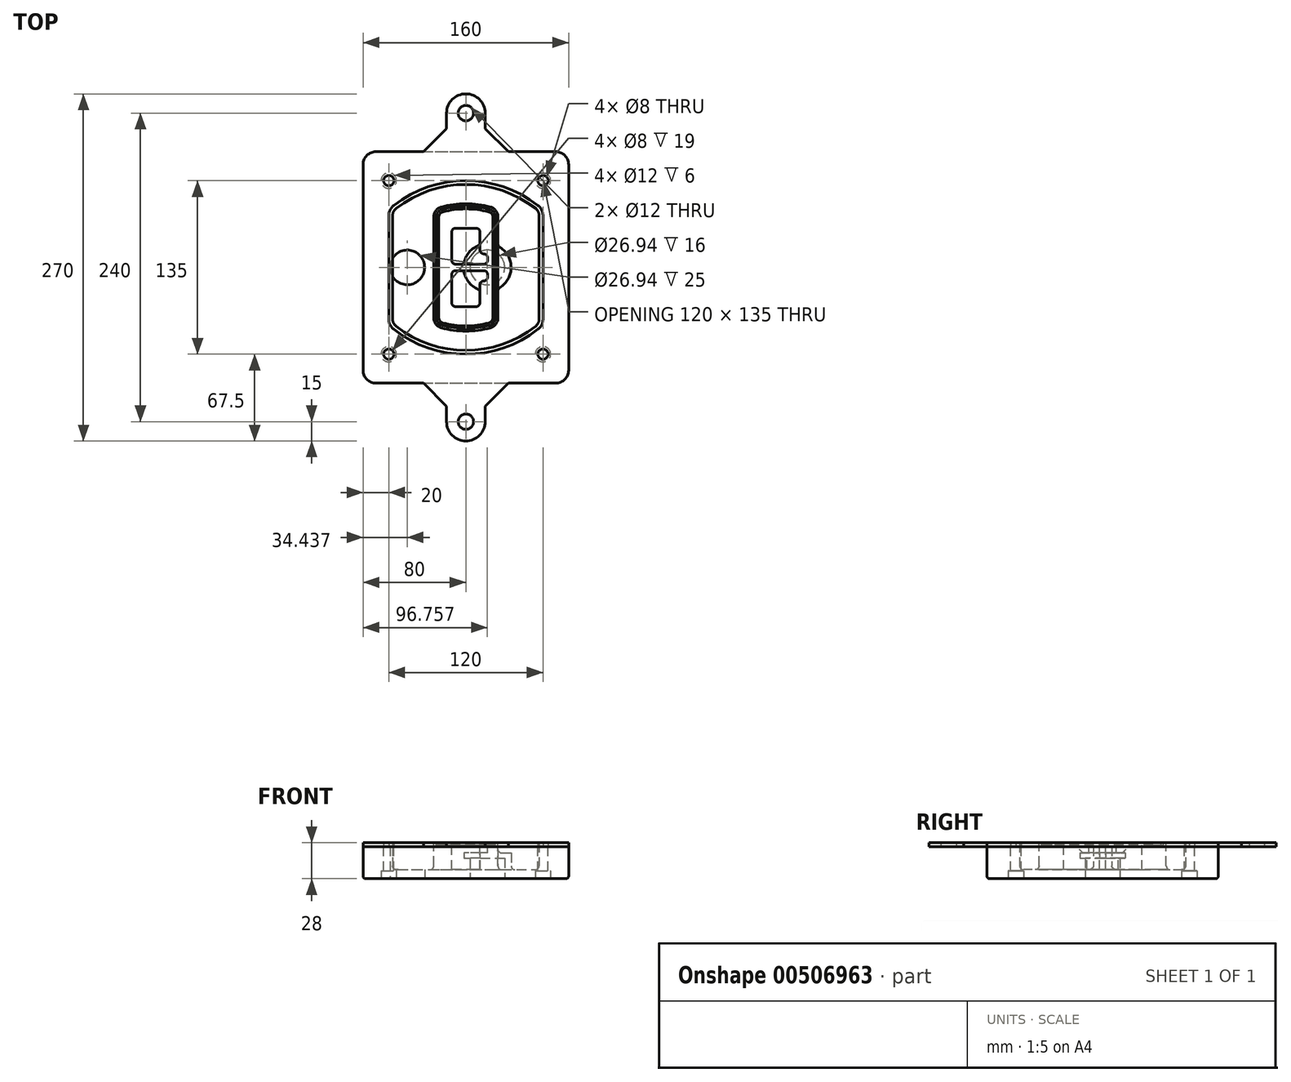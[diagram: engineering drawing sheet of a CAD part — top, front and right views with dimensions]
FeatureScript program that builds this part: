
annotation { "Feature Type Name" : "Feature", "Feature Type Description" : "" }
export const myFeature = defineFeature(function(context is Context, id is Id, definition is map)
    precondition{}
    {
        {
            var Q0;
            Q0=qCreatedBy(makeId("Top.planeOp"),FACE);
            var sketch = newSketch(context, id + "F0", { "sketchPlane" : qUnion([Q0])});
            skPoint(sketch, "E0.rect.middle", {"position": v(0, 0) * mm});
            skLineSegment(sketch, "E1.bottom", {"start": v(-70, -90) * mm, "end": v(70, -90) * mm});
            skLineSegment(sketch, "E1.top", {"start": v(-70, 90) * mm, "end": v(70, 90) * mm});
            skLineSegment(sketch, "E1.left", {"start": v(-80, -80) * mm, "end": v(-80, 80) * mm});
            skLineSegment(sketch, "E1.right", {"start": v(80, -80) * mm, "end": v(80, 80) * mm});
            skLineSegment(sketch, "E2", {"start": v(-80, 90) * mm, "end": v(80, -90) * mm, "construction": true});
            skLineSegment(sketch, "E3", {"start": v(80, 90) * mm, "end": v(-80, -90) * mm, "construction": true});
            skCircle(sketch, "E4", {"center": v(-60, 67.5) * mm, "radius": 4 * mm});
            skCircle(sketch, "E5", {"center": v(60, 67.5) * mm, "radius": 4 * mm});
            skCircle(sketch, "E6", {"center": v(60, -67.5) * mm, "radius": 4 * mm});
            skCircle(sketch, "E7", {"center": v(-60, -67.5) * mm, "radius": 4 * mm});
            skLineSegment(sketch, "E8", {"start": v(-60, 67.5) * mm, "end": v(60, 67.5) * mm, "construction": true});
            skLineSegment(sketch, "E9", {"start": v(60, 67.5) * mm, "end": v(60, -67.5) * mm, "construction": true});
            skLineSegment(sketch, "E10", {"start": v(60, -67.5) * mm, "end": v(-60, -67.5) * mm, "construction": true});
            skLineSegment(sketch, "E11", {"start": v(-60, -67.5) * mm, "end": v(-60, 67.5) * mm, "construction": true});
            skLineSegment(sketch, "E12", {"start": v(-60, 40.3) * mm, "end": v(-60, -40.3) * mm});
            skLineSegment(sketch, "E13", {"start": v(60, 40.3) * mm, "end": v(60, -40.3) * mm});
            skArc(sketch, "E14", {"start": v(56.15, 48.18) * mm, "mid": v(0, 67.5) * mm, "end": v(-56.15, 48.18) * mm});
            skArc(sketch, "E15", {"start": v(-56.15, -48.18) * mm, "mid": v(0, -67.5) * mm, "end": v(56.15, -48.18) * mm});
            skLineSegment(sketch, "E16", {"start": v(-60, 0) * mm, "end": v(60, 0) * mm, "construction": true});
            skPoint(sketch, "E17.visualSharp", {"position": v(-60, -45) * mm});
            skArc(sketch, "E17.filletArc", {"start": v(-60, -40.3) * mm, "mid": v(-58.99, -44.68) * mm, "end": v(-56.15, -48.18) * mm});
            skPoint(sketch, "E18.visualSharp", {"position": v(-60, 45) * mm});
            skArc(sketch, "E18.filletArc", {"start": v(-56.15, 48.18) * mm, "mid": v(-58.99, 44.68) * mm, "end": v(-60, 40.3) * mm});
            skPoint(sketch, "E19.visualSharp", {"position": v(60, 45) * mm});
            skArc(sketch, "E19.filletArc", {"start": v(60, 40.3) * mm, "mid": v(58.99, 44.68) * mm, "end": v(56.15, 48.18) * mm});
            skPoint(sketch, "E20.visualSharp", {"position": v(60, -45) * mm});
            skArc(sketch, "E20.filletArc", {"start": v(56.15, -48.18) * mm, "mid": v(58.99, -44.68) * mm, "end": v(60, -40.3) * mm});
            skPoint(sketch, "E21.visualSharp", {"position": v(-80, 90) * mm});
            skArc(sketch, "E21.filletArc", {"start": v(-70, 90) * mm, "mid": v(-77.07, 87.07) * mm, "end": v(-80, 80) * mm});
            skPoint(sketch, "E22.visualSharp", {"position": v(80, 90) * mm});
            skArc(sketch, "E22.filletArc", {"start": v(80, 80) * mm, "mid": v(77.07, 87.07) * mm, "end": v(70, 90) * mm});
            skPoint(sketch, "E23.visualSharp", {"position": v(80, -90) * mm});
            skArc(sketch, "E23.filletArc", {"start": v(70, -90) * mm, "mid": v(77.07, -87.07) * mm, "end": v(80, -80) * mm});
            skPoint(sketch, "E24.visualSharp", {"position": v(-80, -90) * mm});
            skArc(sketch, "E24.filletArc", {"start": v(-80, -80) * mm, "mid": v(-77.07, -87.07) * mm, "end": v(-70, -90) * mm});
            skArc(sketch, "E25.0", {"start": v(57, 40.3) * mm, "mid": v(56.3, 43.36) * mm, "end": v(54.3, 45.81) * mm});
            skLineSegment(sketch, "E25.1", {"start": v(57, 40.3) * mm, "end": v(57, -40.3) * mm});
            skArc(sketch, "E25.2", {"start": v(54.3, -45.81) * mm, "mid": v(56.3, -43.36) * mm, "end": v(57, -40.3) * mm});
            skArc(sketch, "E25.3", {"start": v(-54.3, -45.81) * mm, "mid": v(0, -64.5) * mm, "end": v(54.3, -45.81) * mm});
            skArc(sketch, "E25.4", {"start": v(-57, -40.3) * mm, "mid": v(-56.3, -43.36) * mm, "end": v(-54.3, -45.81) * mm});
            skArc(sketch, "E25.5", {"start": v(54.3, 45.81) * mm, "mid": v(0, 64.5) * mm, "end": v(-54.3, 45.81) * mm});
            skLineSegment(sketch, "E25.6", {"start": v(-57, 40.3) * mm, "end": v(-57, -40.3) * mm});
            skArc(sketch, "E25.7", {"start": v(-54.3, 45.81) * mm, "mid": v(-56.3, 43.36) * mm, "end": v(-57, 40.3) * mm});
            skArc(sketch, "E26.0", {"start": v(-58.62, 51.33) * mm, "mid": v(-62.58, 46.43) * mm, "end": v(-64, 40.3) * mm});
            skArc(sketch, "E26.1", {"start": v(58.62, 51.33) * mm, "mid": v(0, 71.5) * mm, "end": v(-58.62, 51.33) * mm});
            skArc(sketch, "E26.2", {"start": v(64, 40.3) * mm, "mid": v(62.58, 46.43) * mm, "end": v(58.62, 51.33) * mm});
            skLineSegment(sketch, "E26.3", {"start": v(64, 40.3) * mm, "end": v(64, -40.3) * mm});
            skArc(sketch, "E26.4", {"start": v(58.62, -51.33) * mm, "mid": v(62.58, -46.43) * mm, "end": v(64, -40.3) * mm});
            skLineSegment(sketch, "E26.5", {"start": v(-64, 40.3) * mm, "end": v(-64, -40.3) * mm});
            skArc(sketch, "E26.6", {"start": v(-58.62, -51.33) * mm, "mid": v(0, -71.5) * mm, "end": v(58.62, -51.33) * mm});
            skArc(sketch, "E26.7", {"start": v(-64, -40.3) * mm, "mid": v(-62.58, -46.43) * mm, "end": v(-58.62, -51.33) * mm});
            skSolve(sketch);
        }
        {
            var Q0;
            Q0=makeQuery(id+"F0.imprint","IMPRINT",FACE,{"disambiguationData":[TD([[makeQuery(id+"F0.imprint","IMPRINT",EDGE,{"derivedFrom":sQuery(id+"F0.wireOp",EDGE,"E1.bottom")}),1.0]])]});
            var Q1;
            Q1=makeQuery(id+"F0.imprint","IMPRINT",FACE,{"disambiguationData":[TD([[makeQuery(id+"F0.imprint","IMPRINT",EDGE,{"derivedFrom":sQuery(id+"F0.wireOp",EDGE,"E12")}),1.0]])]});
            var Q2;
            Q2=makeQuery(id+"F0.imprint","IMPRINT",FACE,{"disambiguationData":[TD([[makeQuery(id+"F0.imprint","IMPRINT",EDGE,{"derivedFrom":sQuery(id+"F0.wireOp",EDGE,"E25.0")}),1.0]])]});
            var Q3;
            Q3=makeQuery(id+"F0.imprint","IMPRINT",FACE,{"disambiguationData":[TD([[makeQuery(id+"F0.imprint","IMPRINT",EDGE,{"derivedFrom":sQuery(id+"F0.wireOp",EDGE,"E12")}),-1.0]])]});
            extrude(context, id + "F1", {"entities" : qUnion([Q0, Q1, Q2, Q3]), "oppositeDirection" : true, "depth" : 25 * mm});
        }
        {
            var Q0;
            Q0=makeQuery(id+"F0.imprint","IMPRINT",FACE,{"disambiguationData":[TD([[makeQuery(id+"F0.imprint","IMPRINT",EDGE,{"derivedFrom":sQuery(id+"F0.wireOp",EDGE,"E12")}),1.0]])]});
            extrude(context, id + "F2", {"entities" : qUnion([Q0]), "operationType" : NewBodyOperationType.ADD, "depth" : 3 * mm});
        }
        {
            var Q0;
            Q0=makeQuery(id+"F0.imprint","IMPRINT",FACE,{"disambiguationData":[TD([[makeQuery(id+"F0.imprint","IMPRINT",EDGE,{"derivedFrom":sQuery(id+"F0.wireOp",EDGE,"E25.0")}),1.0]])]});
            extrude(context, id + "F3", {"entities" : qUnion([Q0]), "operationType" : NewBodyOperationType.REMOVE, "oppositeDirection" : true, "depth" : 18 * mm});
        }
        {
            var Q0;
            Q0=makeQuery(id+"F2.opExtrude","CAP_FACE",FACE,{"disambiguationData":[OSD([sQuery(id+"F0.wireOp",EDGE,"E12"),sQuery(id+"F0.wireOp",EDGE,"E13"),sQuery(id+"F0.wireOp",EDGE,"E14"),sQuery(id+"F0.wireOp",EDGE,"E15"),sQuery(id+"F0.wireOp",EDGE,"E17.filletArc"),sQuery(id+"F0.wireOp",EDGE,"E18.filletArc"),sQuery(id+"F0.wireOp",EDGE,"E19.filletArc"),sQuery(id+"F0.wireOp",EDGE,"E20.filletArc"),sQuery(id+"F0.wireOp",EDGE,"E25.0"),sQuery(id+"F0.wireOp",EDGE,"E25.1"),sQuery(id+"F0.wireOp",EDGE,"E25.2"),sQuery(id+"F0.wireOp",EDGE,"E25.3"),sQuery(id+"F0.wireOp",EDGE,"E25.4"),sQuery(id+"F0.wireOp",EDGE,"E25.5"),sQuery(id+"F0.wireOp",EDGE,"E25.6"),sQuery(id+"F0.wireOp",EDGE,"E25.7")])],"isStart":false});
            var sketch = newSketch(context, id + "F4", { "sketchPlane" : qUnion([Q0])});
            skArc(sketch, "E27.0", {"start": v(-19.08, -46.97) * mm, "mid": v(0, -49.5) * mm, "end": v(19.08, -46.97) * mm});
            skArc(sketch, "E28.0", {"start": v(19.08, 46.97) * mm, "mid": v(0, 49.5) * mm, "end": v(-19.08, 46.97) * mm});
            skLineSegment(sketch, "E29", {"start": v(-25, 39.25) * mm, "end": v(-25, -39.25) * mm});
            skLineSegment(sketch, "E30", {"start": v(25, 39.25) * mm, "end": v(25, -39.25) * mm});
            skLineSegment(sketch, "E31", {"start": v(-25, 45.1) * mm, "end": v(25, 45.1) * mm, "construction": true});
            skLineSegment(sketch, "E32", {"start": v(-25, -45.1) * mm, "end": v(25, -45.1) * mm, "construction": true});
            skPoint(sketch, "E33.visualSharp", {"position": v(-25, 45.1) * mm});
            skArc(sketch, "E33.filletArc", {"start": v(-19.08, 46.97) * mm, "mid": v(-23.35, 44.11) * mm, "end": v(-25, 39.25) * mm});
            skPoint(sketch, "E34.visualSharp", {"position": v(25, 45.1) * mm});
            skArc(sketch, "E34.filletArc", {"start": v(25, 39.25) * mm, "mid": v(23.35, 44.11) * mm, "end": v(19.08, 46.97) * mm});
            skPoint(sketch, "E35.visualSharp", {"position": v(25, -45.1) * mm});
            skArc(sketch, "E35.filletArc", {"start": v(19.08, -46.97) * mm, "mid": v(23.35, -44.11) * mm, "end": v(25, -39.25) * mm});
            skPoint(sketch, "E36.visualSharp", {"position": v(-25, -45.1) * mm});
            skArc(sketch, "E36.filletArc", {"start": v(-25, -39.25) * mm, "mid": v(-23.35, -44.11) * mm, "end": v(-19.08, -46.97) * mm});
            skArc(sketch, "E37.0", {"start": v(54.3, 45.81) * mm, "mid": v(0, 64.5) * mm, "end": v(-54.3, 45.81) * mm});
            skArc(sketch, "E37.1", {"start": v(-54.3, 45.81) * mm, "mid": v(-56.3, 43.36) * mm, "end": v(-57, 40.3) * mm});
            skLineSegment(sketch, "E37.2", {"start": v(-57, 40.3) * mm, "end": v(-57, -40.3) * mm});
            skArc(sketch, "E37.3", {"start": v(-57, -40.3) * mm, "mid": v(-56.3, -43.36) * mm, "end": v(-54.3, -45.81) * mm});
            skArc(sketch, "E37.4", {"start": v(-54.3, -45.81) * mm, "mid": v(0, -64.5) * mm, "end": v(54.3, -45.81) * mm});
            skArc(sketch, "E37.5", {"start": v(54.3, -45.81) * mm, "mid": v(56.3, -43.36) * mm, "end": v(57, -40.3) * mm});
            skLineSegment(sketch, "E37.6", {"start": v(57, 40.3) * mm, "end": v(57, -40.3) * mm});
            skArc(sketch, "E37.7", {"start": v(57, 40.3) * mm, "mid": v(56.3, 43.36) * mm, "end": v(54.3, 45.81) * mm});
            skLineSegment(sketch, "E38.0", {"start": v(23, 39.25) * mm, "end": v(23, -39.25) * mm});
            skArc(sketch, "E38.1", {"start": v(18.56, -45.04) * mm, "mid": v(21.76, -42.9) * mm, "end": v(23, -39.25) * mm});
            skArc(sketch, "E38.2", {"start": v(-18.56, -45.04) * mm, "mid": v(0, -47.5) * mm, "end": v(18.56, -45.04) * mm});
            skArc(sketch, "E38.3", {"start": v(-23, -39.25) * mm, "mid": v(-21.76, -42.9) * mm, "end": v(-18.56, -45.04) * mm});
            skLineSegment(sketch, "E38.4", {"start": v(-23, 39.25) * mm, "end": v(-23, -39.25) * mm});
            skArc(sketch, "E38.5", {"start": v(23, 39.25) * mm, "mid": v(21.76, 42.9) * mm, "end": v(18.56, 45.04) * mm});
            skArc(sketch, "E38.6", {"start": v(-18.56, 45.04) * mm, "mid": v(-21.76, 42.9) * mm, "end": v(-23, 39.25) * mm});
            skArc(sketch, "E38.7", {"start": v(18.56, 45.04) * mm, "mid": v(0, 47.5) * mm, "end": v(-18.56, 45.04) * mm});
            skArc(sketch, "E39.0", {"start": v(21, 39.25) * mm, "mid": v(20.18, 41.68) * mm, "end": v(18.04, 43.1) * mm});
            skLineSegment(sketch, "E39.1", {"start": v(21, 39.25) * mm, "end": v(21, -39.25) * mm});
            skArc(sketch, "E39.2", {"start": v(18.04, -43.1) * mm, "mid": v(20.18, -41.68) * mm, "end": v(21, -39.25) * mm});
            skArc(sketch, "E39.3", {"start": v(-18.04, -43.1) * mm, "mid": v(0, -45.5) * mm, "end": v(18.04, -43.1) * mm});
            skArc(sketch, "E39.4", {"start": v(-21, -39.25) * mm, "mid": v(-20.18, -41.68) * mm, "end": v(-18.04, -43.1) * mm});
            skArc(sketch, "E39.5", {"start": v(18.04, 43.1) * mm, "mid": v(0, 45.5) * mm, "end": v(-18.04, 43.1) * mm});
            skLineSegment(sketch, "E39.6", {"start": v(-21, 39.25) * mm, "end": v(-21, -39.25) * mm});
            skArc(sketch, "E39.7", {"start": v(-18.04, 43.1) * mm, "mid": v(-20.18, 41.68) * mm, "end": v(-21, 39.25) * mm});
            skLineSegment(sketch, "E40", {"start": v(-25, 0) * mm, "end": v(25, 0) * mm, "construction": true});
            skLineSegment(sketch, "E41", {"start": v(-11, 5.5) * mm, "end": v(-11, 27.5) * mm});
            skLineSegment(sketch, "E42", {"start": v(-8, 30.5) * mm, "end": v(8, 30.5) * mm});
            skLineSegment(sketch, "E43", {"start": v(11, 27.5) * mm, "end": v(11, 13.5) * mm});
            skLineSegment(sketch, "E44", {"start": v(14, 10.5) * mm, "end": v(14, 10.5) * mm});
            skLineSegment(sketch, "E45", {"start": v(17, 7.5) * mm, "end": v(17, 5.5) * mm});
            skLineSegment(sketch, "E46", {"start": v(14, 2.5) * mm, "end": v(-8, 2.5) * mm});
            skPoint(sketch, "E47.visualSharp", {"position": v(-11, 30.5) * mm});
            skArc(sketch, "E47.filletArc", {"start": v(-8, 30.5) * mm, "mid": v(-10.12, 29.62) * mm, "end": v(-11, 27.5) * mm});
            skPoint(sketch, "E48.visualSharp", {"position": v(11, 30.5) * mm});
            skArc(sketch, "E48.filletArc", {"start": v(11, 27.5) * mm, "mid": v(10.12, 29.62) * mm, "end": v(8, 30.5) * mm});
            skPoint(sketch, "E49.visualSharp", {"position": v(11, 10.5) * mm});
            skArc(sketch, "E49.filletArc", {"start": v(11, 13.5) * mm, "mid": v(11.88, 11.38) * mm, "end": v(14, 10.5) * mm});
            skPoint(sketch, "E50.visualSharp", {"position": v(17, 10.5) * mm});
            skArc(sketch, "E50.filletArc", {"start": v(17, 7.5) * mm, "mid": v(16.12, 9.62) * mm, "end": v(14, 10.5) * mm});
            skPoint(sketch, "E51.visualSharp", {"position": v(17, 2.5) * mm});
            skArc(sketch, "E51.filletArc", {"start": v(14, 2.5) * mm, "mid": v(16.12, 3.38) * mm, "end": v(17, 5.5) * mm});
            skPoint(sketch, "E52.visualSharp", {"position": v(-11, 2.5) * mm});
            skArc(sketch, "E52.filletArc", {"start": v(-11, 5.5) * mm, "mid": v(-10.12, 3.38) * mm, "end": v(-8, 2.5) * mm});
            skLineSegment(sketch, "E53.0.MirrorCS", {"start": v(14, -2.5) * mm, "end": v(-8, -2.5) * mm});
            skArc(sketch, "E54.0.MirrorCS", {"start": v(-11, -5.5) * mm, "mid": v(-10.12, -3.38) * mm, "end": v(-8, -2.5) * mm});
            skLineSegment(sketch, "E55.0.MirrorCS", {"start": v(-11, -5.5) * mm, "end": v(-11, -27.5) * mm});
            skArc(sketch, "E56.0.MirrorCS", {"start": v(-8, -30.5) * mm, "mid": v(-10.12, -29.62) * mm, "end": v(-11, -27.5) * mm});
            skLineSegment(sketch, "E57.0.MirrorCS", {"start": v(-8, -30.5) * mm, "end": v(8, -30.5) * mm});
            skArc(sketch, "E58.0.MirrorCS", {"start": v(11, -27.5) * mm, "mid": v(10.12, -29.62) * mm, "end": v(8, -30.5) * mm});
            skLineSegment(sketch, "E59.0.MirrorCS", {"start": v(11, -27.5) * mm, "end": v(11, -13.5) * mm});
            skArc(sketch, "E60.0.MirrorCS", {"start": v(11, -13.5) * mm, "mid": v(11.88, -11.38) * mm, "end": v(14, -10.5) * mm});
            skArc(sketch, "E61.0.MirrorCS", {"start": v(17, -7.5) * mm, "mid": v(16.12, -9.62) * mm, "end": v(14, -10.5) * mm});
            skLineSegment(sketch, "E62.0.MirrorCS", {"start": v(17, -7.5) * mm, "end": v(17, -5.5) * mm});
            skArc(sketch, "E63.0.MirrorCS", {"start": v(14, -2.5) * mm, "mid": v(16.12, -3.38) * mm, "end": v(17, -5.5) * mm});
            skSolve(sketch);
        }
        {
            var Q0;
            Q0=makeQuery(id+"F4.imprint","IMPRINT",FACE,{"disambiguationData":[TD([[makeQuery(id+"F4.imprint","IMPRINT",EDGE,{"derivedFrom":sQuery(id+"F4.wireOp",EDGE,"E27.0")}),1.0]])]});
            var Q1;
            Q1=makeQuery(id+"F4.imprint","IMPRINT",FACE,{"disambiguationData":[TD([[makeQuery(id+"F4.imprint","IMPRINT",EDGE,{"derivedFrom":sQuery(id+"F4.wireOp",EDGE,"E38.0")}),-1.0]])]});
            var Q2;
            Q2=makeQuery(id+"F4.imprint","IMPRINT",FACE,{"disambiguationData":[TD([[makeQuery(id+"F4.imprint","IMPRINT",EDGE,{"derivedFrom":sQuery(id+"F4.wireOp",EDGE,"E39.0")}),1.0]])]});
            extrude(context, id + "F5", {"entities" : qUnion([Q0, Q1, Q2]), "operationType" : NewBodyOperationType.ADD, "endBound" : BoundingType.UP_TO_NEXT, "oppositeDirection" : true, "depth" : 25 * mm});
        }
        {
            var Q0;
            Q0=makeQuery(id+"F4.imprint","IMPRINT",FACE,{"disambiguationData":[TD([[makeQuery(id+"F4.imprint","IMPRINT",EDGE,{"derivedFrom":sQuery(id+"F4.wireOp",EDGE,"E38.0")}),-1.0]])]});
            extrude(context, id + "F6", {"entities" : qUnion([Q0]), "operationType" : NewBodyOperationType.REMOVE, "oppositeDirection" : true, "depth" : 2 * mm});
        }
        {
            var Q0;
            Q0=makeQuery(id+"F1.opExtrude","CAP_FACE",FACE,{"disambiguationData":[OSD([sQuery(id+"F0.wireOp",EDGE,"E1.bottom"),sQuery(id+"F0.wireOp",EDGE,"E1.top"),sQuery(id+"F0.wireOp",EDGE,"E1.left"),sQuery(id+"F0.wireOp",EDGE,"E1.right"),sQuery(id+"F0.wireOp",EDGE,"E4"),sQuery(id+"F0.wireOp",EDGE,"E5"),sQuery(id+"F0.wireOp",EDGE,"E6"),sQuery(id+"F0.wireOp",EDGE,"E7"),sQuery(id+"F0.wireOp",EDGE,"E21.filletArc"),sQuery(id+"F0.wireOp",EDGE,"E22.filletArc"),sQuery(id+"F0.wireOp",EDGE,"E23.filletArc"),sQuery(id+"F0.wireOp",EDGE,"E24.filletArc")])],"isStart":false});
            var sketch = newSketch(context, id + "F7", { "sketchPlane" : qUnion([Q0])});
            skCircle(sketch, "E64", {"center": v(16.76, 0) * mm, "radius": 13.47 * mm});
            skCircle(sketch, "E65", {"center": v(-45.56, 0) * mm, "radius": 13.47 * mm});
            skLineSegment(sketch, "E66", {"start": v(80, 0) * mm, "end": v(-80, 0) * mm});
            skCircle(sketch, "E67", {"center": v(16.76, 0) * mm, "radius": 18.47 * mm});
            skCircle(sketch, "E68", {"center": v(60, -67.5) * mm, "radius": 6 * mm});
            skCircle(sketch, "E69", {"center": v(-60, -67.5) * mm, "radius": 6 * mm});
            skCircle(sketch, "E70", {"center": v(-60, 67.5) * mm, "radius": 6 * mm});
            skCircle(sketch, "E71", {"center": v(60, 67.5) * mm, "radius": 6 * mm});
            skSolve(sketch);
        }
        {
            var Q0;
            {var subQ1=sQuery(id+"F7.wireOp",EDGE,"E66");var subQ4=sQuery(id+"F7.wireOp",EDGE,"E64");var subQ6=makeQuery(id+"F7.imprint","INTERSECT",VERTEX,{"disambiguationData":[OD(0.0)],"derivedFrom":[subQ4,subQ1]});Q0=makeQuery(id+"F7.imprint","IMPRINT",FACE,{"disambiguationData":[TD([[makeQuery(id+"F7.imprint","IMPRINT",EDGE,{"disambiguationData":[TD([[subQ6,-1.0]])],"derivedFrom":subQ4}),-1.0]])]});}
            var Q1;
            {var subQ0=sQuery(id+"F7.wireOp",EDGE,"E66");var subQ1=sQuery(id+"F7.wireOp",EDGE,"E64");var subQ3=makeQuery(id+"F7.imprint","INTERSECT",VERTEX,{"disambiguationData":[OD(0.0)],"derivedFrom":[subQ1,subQ0]});Q1=makeQuery(id+"F7.imprint","IMPRINT",FACE,{"disambiguationData":[TD([[makeQuery(id+"F7.imprint","IMPRINT",EDGE,{"disambiguationData":[TD([[subQ3,-1.0]])],"derivedFrom":subQ1}),1.0]])]});}
            var Q2;
            {var subQ0=sQuery(id+"F7.wireOp",EDGE,"E66");var subQ1=sQuery(id+"F7.wireOp",EDGE,"E64");var subQ3=makeQuery(id+"F7.imprint","INTERSECT",VERTEX,{"disambiguationData":[OD(0.0)],"derivedFrom":[subQ1,subQ0]});Q2=makeQuery(id+"F7.imprint","IMPRINT",FACE,{"disambiguationData":[TD([[makeQuery(id+"F7.imprint","IMPRINT",EDGE,{"disambiguationData":[TD([[subQ3,1.0]])],"derivedFrom":subQ1}),1.0]])]});}
            var Q3;
            {var subQ1=sQuery(id+"F7.wireOp",EDGE,"E66");var subQ4=sQuery(id+"F7.wireOp",EDGE,"E64");var subQ6=makeQuery(id+"F7.imprint","INTERSECT",VERTEX,{"disambiguationData":[OD(0.0)],"derivedFrom":[subQ4,subQ1]});Q3=makeQuery(id+"F7.imprint","IMPRINT",FACE,{"disambiguationData":[TD([[makeQuery(id+"F7.imprint","IMPRINT",EDGE,{"disambiguationData":[TD([[subQ6,1.0]])],"derivedFrom":subQ4}),-1.0]])]});}
            extrude(context, id + "F8", {"entities" : qUnion([Q0, Q1, Q2, Q3]), "operationType" : NewBodyOperationType.ADD, "oppositeDirection" : true, "depth" : 20 * mm});
        }
        {
            var Q0;
            {var subQ0=sQuery(id+"F7.wireOp",EDGE,"E66");var subQ1=sQuery(id+"F7.wireOp",EDGE,"E64");var subQ3=makeQuery(id+"F7.imprint","INTERSECT",VERTEX,{"disambiguationData":[OD(0.0)],"derivedFrom":[subQ1,subQ0]});Q0=makeQuery(id+"F7.imprint","IMPRINT",FACE,{"disambiguationData":[TD([[makeQuery(id+"F7.imprint","IMPRINT",EDGE,{"disambiguationData":[TD([[subQ3,-1.0]])],"derivedFrom":subQ1}),1.0]])]});}
            var Q1;
            {var subQ0=sQuery(id+"F7.wireOp",EDGE,"E66");var subQ1=sQuery(id+"F7.wireOp",EDGE,"E64");var subQ3=makeQuery(id+"F7.imprint","INTERSECT",VERTEX,{"disambiguationData":[OD(0.0)],"derivedFrom":[subQ1,subQ0]});Q1=makeQuery(id+"F7.imprint","IMPRINT",FACE,{"disambiguationData":[TD([[makeQuery(id+"F7.imprint","IMPRINT",EDGE,{"disambiguationData":[TD([[subQ3,1.0]])],"derivedFrom":subQ1}),1.0]])]});}
            extrude(context, id + "F9", {"entities" : qUnion([Q0, Q1]), "operationType" : NewBodyOperationType.REMOVE, "oppositeDirection" : true, "depth" : 16 * mm});
        }
        {
            var Q0;
            {var subQ0=sQuery(id+"F7.wireOp",EDGE,"E66");var subQ1=sQuery(id+"F7.wireOp",EDGE,"E65");var subQ3=makeQuery(id+"F7.imprint","INTERSECT",VERTEX,{"disambiguationData":[OD(0.0)],"derivedFrom":[subQ1,subQ0]});Q0=makeQuery(id+"F7.imprint","IMPRINT",FACE,{"disambiguationData":[TD([[makeQuery(id+"F7.imprint","IMPRINT",EDGE,{"disambiguationData":[TD([[subQ3,-1.0]])],"derivedFrom":subQ1}),1.0]])]});}
            var Q1;
            {var subQ0=sQuery(id+"F7.wireOp",EDGE,"E66");var subQ1=sQuery(id+"F7.wireOp",EDGE,"E65");var subQ3=makeQuery(id+"F7.imprint","INTERSECT",VERTEX,{"disambiguationData":[OD(0.0)],"derivedFrom":[subQ1,subQ0]});Q1=makeQuery(id+"F7.imprint","IMPRINT",FACE,{"disambiguationData":[TD([[makeQuery(id+"F7.imprint","IMPRINT",EDGE,{"disambiguationData":[TD([[subQ3,1.0]])],"derivedFrom":subQ1}),1.0]])]});}
            extrude(context, id + "F10", {"entities" : qUnion([Q0, Q1]), "operationType" : NewBodyOperationType.REMOVE, "oppositeDirection" : true, "depth" : 25 * mm});
        }
        {
            var Q0;
            Q0=makeQuery(id+"F7.imprint","IMPRINT",FACE,{"disambiguationData":[TD([[makeQuery(id+"F7.imprint","IMPRINT",EDGE,{"derivedFrom":sQuery(id+"F7.wireOp",EDGE,"E68")}),1.0]])]});
            var Q1;
            Q1=makeQuery(id+"F7.imprint","IMPRINT",FACE,{"disambiguationData":[TD([[makeQuery(id+"F7.imprint","IMPRINT",EDGE,{"derivedFrom":makeQuery(id+"F1.opExtrude","CAP_EDGE",EDGE,{"disambiguationData":[OSD([sQuery(id+"F0.wireOp",EDGE,"E5")])],"isStart":false})}),-1.0]])]});
            var Q2;
            Q2=makeQuery(id+"F7.imprint","IMPRINT",FACE,{"disambiguationData":[TD([[makeQuery(id+"F7.imprint","IMPRINT",EDGE,{"derivedFrom":sQuery(id+"F7.wireOp",EDGE,"E69")}),1.0]])]});
            var Q3;
            Q3=makeQuery(id+"F7.imprint","IMPRINT",FACE,{"disambiguationData":[TD([[makeQuery(id+"F7.imprint","IMPRINT",EDGE,{"derivedFrom":makeQuery(id+"F1.opExtrude","CAP_EDGE",EDGE,{"disambiguationData":[OSD([sQuery(id+"F0.wireOp",EDGE,"E4")])],"isStart":false})}),-1.0]])]});
            var Q4;
            Q4=makeQuery(id+"F7.imprint","IMPRINT",FACE,{"disambiguationData":[TD([[makeQuery(id+"F7.imprint","IMPRINT",EDGE,{"derivedFrom":sQuery(id+"F7.wireOp",EDGE,"E70")}),1.0]])]});
            var Q5;
            Q5=makeQuery(id+"F7.imprint","IMPRINT",FACE,{"disambiguationData":[TD([[makeQuery(id+"F7.imprint","IMPRINT",EDGE,{"derivedFrom":makeQuery(id+"F1.opExtrude","CAP_EDGE",EDGE,{"disambiguationData":[OSD([sQuery(id+"F0.wireOp",EDGE,"E7")])],"isStart":false})}),-1.0]])]});
            var Q6;
            Q6=makeQuery(id+"F7.imprint","IMPRINT",FACE,{"disambiguationData":[TD([[makeQuery(id+"F7.imprint","IMPRINT",EDGE,{"derivedFrom":sQuery(id+"F7.wireOp",EDGE,"E71")}),1.0]])]});
            var Q7;
            Q7=makeQuery(id+"F7.imprint","IMPRINT",FACE,{"disambiguationData":[TD([[makeQuery(id+"F7.imprint","IMPRINT",EDGE,{"derivedFrom":makeQuery(id+"F1.opExtrude","CAP_EDGE",EDGE,{"disambiguationData":[OSD([sQuery(id+"F0.wireOp",EDGE,"E6")])],"isStart":false})}),-1.0]])]});
            extrude(context, id + "F11", {"entities" : qUnion([Q0, Q1, Q2, Q3, Q4, Q5, Q6, Q7]), "operationType" : NewBodyOperationType.REMOVE, "oppositeDirection" : true, "depth" : 6 * mm});
        }
        {
            var Q0;
            Q0=makeQuery(id+"F9.boolean.opBoolean","COPY",FACE,{"derivedFrom":makeQuery(id+"F9.opExtrude","CAP_FACE",FACE,{"disambiguationData":[OSD([sQuery(id+"F7.wireOp",EDGE,"E64")])],"isStart":false})});
            var sketch = newSketch(context, id + "F12", { "sketchPlane" : qUnion([Q0])});
            skArc(sketch, "E72.0", {"start": v(11, 17.55) * mm, "mid": v(2.57, 11.82) * mm, "end": v(-1.54, 2.5) * mm});
            skArc(sketch, "E72.1", {"start": v(-1.54, -2.5) * mm, "mid": v(2.57, -11.82) * mm, "end": v(11, -17.55) * mm});
            skLineSegment(sketch, "E73", {"start": v(-1.54, -2.5) * mm, "end": v(14, -2.5) * mm});
            skLineSegment(sketch, "E74.0", {"start": v(14, 2.5) * mm, "end": v(-1.54, 2.5) * mm});
            skArc(sketch, "E74.1", {"start": v(14, 2.5) * mm, "mid": v(16.12, 3.38) * mm, "end": v(17, 5.5) * mm});
            skLineSegment(sketch, "E74.2", {"start": v(17, 7.5) * mm, "end": v(17, 5.5) * mm});
            skArc(sketch, "E74.3", {"start": v(17, 7.5) * mm, "mid": v(16.12, 9.62) * mm, "end": v(14, 10.5) * mm});
            skArc(sketch, "E74.4", {"start": v(11, 13.5) * mm, "mid": v(11.88, 11.38) * mm, "end": v(14, 10.5) * mm});
            skLineSegment(sketch, "E74.5", {"start": v(11, 17.55) * mm, "end": v(11, 13.5) * mm});
            skLineSegment(sketch, "E74.7", {"start": v(14, -2.5) * mm, "end": v(-1.54, -2.5) * mm});
            skArc(sketch, "E74.8", {"start": v(14, -2.5) * mm, "mid": v(16.12, -3.38) * mm, "end": v(17, -5.5) * mm});
            skLineSegment(sketch, "E74.9", {"start": v(17, -7.5) * mm, "end": v(17, -5.5) * mm});
            skArc(sketch, "E74.10", {"start": v(17, -7.5) * mm, "mid": v(16.12, -9.62) * mm, "end": v(14, -10.5) * mm});
            skArc(sketch, "E74.11", {"start": v(11, -13.5) * mm, "mid": v(11.88, -11.38) * mm, "end": v(14, -10.5) * mm});
            skLineSegment(sketch, "E74.12", {"start": v(11, -17.55) * mm, "end": v(11, -13.5) * mm});
            skPoint(sketch, "E75.orphan", {"position": v(11, -27.5) * mm});
            skPoint(sketch, "E76.orphan", {"position": v(-8, -2.5) * mm});
            skPoint(sketch, "E77.orphan", {"position": v(-8, 2.5) * mm});
            skPoint(sketch, "E78.orphan", {"position": v(11, 27.5) * mm});
            skSolve(sketch);
        }
        {
            var Q0;
            {var subQ7=sQuery(id+"F12.wireOp",EDGE,"E72.0");var subQ14=sQuery(id+"F12.wireOp",EDGE,"E72.1");var subQ16=sQuery(id+"F12.wireOp",EDGE,"E74.1");var subQ18=sQuery(id+"F12.wireOp",EDGE,"E74.8");Q0=qUnion([makeQuery(id+"F12.imprint","IMPRINT",FACE,{"disambiguationData":[TD([[makeQuery(id+"F12.imprint","IMPRINT",EDGE,{"derivedFrom":subQ7}),1.0]])]}),makeQuery(id+"F12.imprint","IMPRINT",FACE,{"disambiguationData":[TD([[makeQuery(id+"F12.imprint","IMPRINT",EDGE,{"derivedFrom":subQ14}),1.0]])]}),makeQuery(id+"F12.imprint","IMPRINT",FACE,{"disambiguationData":[TD([[makeQuery(id+"F12.imprint","IMPRINT",EDGE,{"derivedFrom":subQ16}),1.0]])]}),makeQuery(id+"F12.imprint","IMPRINT",FACE,{"disambiguationData":[TD([[makeQuery(id+"F12.imprint","IMPRINT",EDGE,{"derivedFrom":subQ18}),-1.0]])]})]);}
            var Q1;
            Q1=makeQuery(id+"F5.boolean.opBoolean","SPLIT",FACE,{"disambiguationData":[TD([makeQuery(id+"F5.opExtrude","SWEPT_FACE",FACE,{"disambiguationData":[OSD([sQuery(id+"F4.wireOp",EDGE,"E41")])]})])],"derivedFrom":makeQuery(id+"F3.boolean.opBoolean","COPY",FACE,{"derivedFrom":makeQuery(id+"F3.opExtrude","CAP_FACE",FACE,{"disambiguationData":[OSD([sQuery(id+"F0.wireOp",EDGE,"E25.0"),sQuery(id+"F0.wireOp",EDGE,"E25.1"),sQuery(id+"F0.wireOp",EDGE,"E25.2"),sQuery(id+"F0.wireOp",EDGE,"E25.3"),sQuery(id+"F0.wireOp",EDGE,"E25.4"),sQuery(id+"F0.wireOp",EDGE,"E25.5"),sQuery(id+"F0.wireOp",EDGE,"E25.6"),sQuery(id+"F0.wireOp",EDGE,"E25.7")])],"isStart":false})})});
            extrude(context, id + "F13", {"entities" : qUnion([Q0]), "operationType" : NewBodyOperationType.REMOVE, "endBound" : BoundingType.UP_TO_SURFACE, "endBoundEntityFace" : qUnion([Q1]), "depth" : 25 * mm});
        }
        {
            var Q0;
            Q0=makeQuery(id+"F3.boolean.opBoolean","COPY",EDGE,{"derivedFrom":makeQuery(id+"F3.opExtrude","CAP_EDGE",EDGE,{"disambiguationData":[OSD([sQuery(id+"F0.wireOp",EDGE,"E25.6")])],"isStart":false})});
            var Q1;
            Q1=makeQuery(id+"F8.boolean.opBoolean","INTERSECT",EDGE,{"derivedFrom":[makeQuery(id+"F5.opExtrude","SWEPT_FACE",FACE,{"disambiguationData":[OSD([sQuery(id+"F4.wireOp",EDGE,"E30")])]}),makeQuery(id+"F8.opExtrude","CAP_FACE",FACE,{"disambiguationData":[OSD([sQuery(id+"F7.wireOp",EDGE,"E67")])],"isStart":false})]});
            var Q2;
            Q2=makeQuery(id+"F8.boolean.opBoolean","INTERSECT",EDGE,{"disambiguationData":[OD(1.0)],"derivedFrom":[makeQuery(id+"F5.opExtrude","SWEPT_FACE",FACE,{"disambiguationData":[OSD([sQuery(id+"F4.wireOp",EDGE,"E30")])]}),makeQuery(id+"F8.opExtrude","SWEPT_FACE",FACE,{"disambiguationData":[OSD([sQuery(id+"F7.wireOp",EDGE,"E67")])]})]});
            var Q3;
            {var subQ0=sQuery(id+"F4.wireOp",EDGE,"E30");Q3=makeQuery(id+"F8.boolean.opBoolean","SPLIT",EDGE,{"disambiguationData":[TD([makeQuery(id+"F5.opExtrude","SWEPT_FACE",FACE,{"disambiguationData":[OSD([sQuery(id+"F4.wireOp",EDGE,"E35.filletArc")])]})])],"derivedFrom":makeQuery(id+"F5.opExtrude","CAP_EDGE",EDGE,{"disambiguationData":[OSD([subQ0])],"isStart":false})});}
            var Q4;
            {var subQ0=sQuery(id+"F0.wireOp",EDGE,"E25.7");var subQ1=sQuery(id+"F0.wireOp",EDGE,"E25.1");var subQ2=sQuery(id+"F0.wireOp",EDGE,"E25.6");var subQ3=sQuery(id+"F0.wireOp",EDGE,"E25.5");var subQ4=sQuery(id+"F0.wireOp",EDGE,"E25.4");var subQ5=sQuery(id+"F0.wireOp",EDGE,"E25.0");var subQ6=sQuery(id+"F0.wireOp",EDGE,"E25.2");var subQ7=sQuery(id+"F0.wireOp",EDGE,"E25.3");Q4=makeQuery(id+"F8.boolean.opBoolean","INTERSECT",EDGE,{"derivedFrom":[makeQuery(id+"F5.boolean.opBoolean","SPLIT",FACE,{"disambiguationData":[TD([makeQuery(id+"F2.opExtrude","SWEPT_FACE",FACE,{"disambiguationData":[OSD([subQ5])]})])],"derivedFrom":makeQuery(id+"F3.boolean.opBoolean","COPY",FACE,{"derivedFrom":makeQuery(id+"F3.opExtrude","CAP_FACE",FACE,{"disambiguationData":[OSD([subQ5,subQ1,subQ6,subQ7,subQ4,subQ3,subQ2,subQ0])],"isStart":false})})}),makeQuery(id+"F8.opExtrude","SWEPT_FACE",FACE,{"disambiguationData":[OSD([sQuery(id+"F7.wireOp",EDGE,"E67")])]})]});}
            var Q5;
            Q5=makeQuery(id+"F8.boolean.opBoolean","INTERSECT",EDGE,{"disambiguationData":[OD(0.0)],"derivedFrom":[makeQuery(id+"F5.opExtrude","SWEPT_FACE",FACE,{"disambiguationData":[OSD([sQuery(id+"F4.wireOp",EDGE,"E30")])]}),makeQuery(id+"F8.opExtrude","SWEPT_FACE",FACE,{"disambiguationData":[OSD([sQuery(id+"F7.wireOp",EDGE,"E67")])]})]});
            fillet(context, id + "F14", {"entities" : qUnion([Q0, Q1, Q2, Q3, Q4, Q5]), "radius" : 3 * mm, "tangentPropagation" : true, "allowEdgeOverflow" : false});
        }
        {
            var Q0;
            Q0=makeQuery(id+"F1.opExtrude","CAP_EDGE",EDGE,{"disambiguationData":[OSD([sQuery(id+"F0.wireOp",EDGE,"E1.bottom")])],"isStart":false});
            fillet(context, id + "F15", {"entities" : qUnion([Q0]), "radius" : 2 * mm, "tangentPropagation" : true, "allowEdgeOverflow" : false});
        }
        {
            var Q0;
            {var subQ0=sQuery(id+"F0.wireOp",EDGE,"E21.filletArc");var subQ1=sQuery(id+"F0.wireOp",EDGE,"E7");var subQ2=sQuery(id+"F0.wireOp",EDGE,"E6");var subQ3=sQuery(id+"F0.wireOp",EDGE,"E5");var subQ4=sQuery(id+"F0.wireOp",EDGE,"E4");var subQ5=sQuery(id+"F0.wireOp",EDGE,"E22.filletArc");var subQ6=sQuery(id+"F0.wireOp",EDGE,"E1.bottom");var subQ7=sQuery(id+"F0.wireOp",EDGE,"E1.right");var subQ8=sQuery(id+"F0.wireOp",EDGE,"E1.top");var subQ9=sQuery(id+"F0.wireOp",EDGE,"E1.left");var subQ10=sQuery(id+"F0.wireOp",EDGE,"E23.filletArc");var subQ11=sQuery(id+"F0.wireOp",EDGE,"E24.filletArc");Q0=makeQuery(id+"F2.boolean.opBoolean","SPLIT",FACE,{"disambiguationData":[TD([makeQuery(id+"F1.opExtrude","SWEPT_FACE",FACE,{"disambiguationData":[OSD([subQ6])]})])],"derivedFrom":makeQuery(id+"F1.opExtrude","CAP_FACE",FACE,{"disambiguationData":[OSD([subQ6,subQ8,subQ9,subQ7,subQ4,subQ3,subQ2,subQ1,subQ0,subQ5,subQ10,subQ11])],"isStart":true})});}
            var sketch = newSketch(context, id + "F16", { "sketchPlane" : qUnion([Q0])});
            skArc(sketch, "E79.0", {"start": v(56.15, 48.18) * mm, "mid": v(0, 67.5) * mm, "end": v(-56.15, 48.18) * mm});
            skCircle(sketch, "E79.1", {"center": v(-60, 67.5) * mm, "radius": 4 * mm});
            skLineSegment(sketch, "E79.2", {"start": v(-70, 90) * mm, "end": v(70, 90) * mm});
            skArc(sketch, "E79.3", {"start": v(-70, 90) * mm, "mid": v(-77.07, 87.07) * mm, "end": v(-80, 80) * mm});
            skLineSegment(sketch, "E79.4", {"start": v(-80, -80) * mm, "end": v(-80, 80) * mm});
            skArc(sketch, "E79.5", {"start": v(-80, -80) * mm, "mid": v(-77.07, -87.07) * mm, "end": v(-70, -90) * mm});
            skCircle(sketch, "E79.6", {"center": v(-60, -67.5) * mm, "radius": 4 * mm});
            skLineSegment(sketch, "E79.7", {"start": v(-70, -90) * mm, "end": v(70, -90) * mm});
            skCircle(sketch, "E79.8", {"center": v(60, -67.5) * mm, "radius": 4 * mm});
            skArc(sketch, "E79.9", {"start": v(70, -90) * mm, "mid": v(77.07, -87.07) * mm, "end": v(80, -80) * mm});
            skLineSegment(sketch, "E79.10", {"start": v(80, -80) * mm, "end": v(80, 80) * mm});
            skArc(sketch, "E79.11", {"start": v(80, 80) * mm, "mid": v(77.07, 87.07) * mm, "end": v(70, 90) * mm});
            skCircle(sketch, "E79.12", {"center": v(60, 67.5) * mm, "radius": 4 * mm});
            skArc(sketch, "E79.13", {"start": v(60, 40.3) * mm, "mid": v(58.99, 44.68) * mm, "end": v(56.15, 48.18) * mm});
            skLineSegment(sketch, "E79.14", {"start": v(60, 40.3) * mm, "end": v(60, -40.3) * mm});
            skArc(sketch, "E79.15", {"start": v(56.15, -48.18) * mm, "mid": v(58.99, -44.68) * mm, "end": v(60, -40.3) * mm});
            skArc(sketch, "E79.16", {"start": v(-56.15, -48.18) * mm, "mid": v(0, -67.5) * mm, "end": v(56.15, -48.18) * mm});
            skArc(sketch, "E79.17", {"start": v(-60, -40.3) * mm, "mid": v(-58.99, -44.68) * mm, "end": v(-56.15, -48.18) * mm});
            skLineSegment(sketch, "E79.18", {"start": v(-60, 40.3) * mm, "end": v(-60, -40.3) * mm});
            skArc(sketch, "E79.19", {"start": v(-56.15, 48.18) * mm, "mid": v(-58.99, 44.68) * mm, "end": v(-60, 40.3) * mm});
            skLineSegment(sketch, "E80", {"start": v(0, 90) * mm, "end": v(0, 120) * mm, "construction": true});
            skPoint(sketch, "E80.endSnap0", {"position": v(0, 90) * mm});
            skLineSegment(sketch, "E81", {"start": v(-33, 90) * mm, "end": v(-15, 108) * mm});
            skLineSegment(sketch, "E82", {"start": v(15, 108) * mm, "end": v(15, 120) * mm});
            skLineSegment(sketch, "E83", {"start": v(-15, 108) * mm, "end": v(-15, 120) * mm});
            skCircle(sketch, "E84", {"center": v(0, 120) * mm, "radius": 6 * mm});
            skArc(sketch, "E85", {"start": v(15, 120) * mm, "mid": v(0, 135) * mm, "end": v(-15, 120) * mm});
            skLineSegment(sketch, "E86", {"start": v(15, 108) * mm, "end": v(33, 90) * mm});
            skLineSegment(sketch, "E87", {"start": v(-80, 0) * mm, "end": v(80, 0) * mm, "construction": true});
            skLineSegment(sketch, "E88.MirrorCS", {"start": v(15, -108) * mm, "end": v(15, -120) * mm});
            skArc(sketch, "E89.MirrorCS", {"start": v(15, -120) * mm, "mid": v(0, -135) * mm, "end": v(-15, -120) * mm});
            skLineSegment(sketch, "E90.MirrorCS", {"start": v(-15, -108) * mm, "end": v(-15, -120) * mm});
            skLineSegment(sketch, "E91.MirrorCS", {"start": v(-33, -90) * mm, "end": v(-15, -108) * mm});
            skLineSegment(sketch, "E92.MirrorCS", {"start": v(0, -90) * mm, "end": v(0, -120) * mm, "construction": true});
            skLineSegment(sketch, "E93.MirrorCS", {"start": v(15, -108) * mm, "end": v(33, -90) * mm});
            skCircle(sketch, "E94.MirrorC", {"center": v(0, -120) * mm, "radius": 6 * mm});
            skSolve(sketch);
        }
        {
            var Q0;
            Q0 = qSketchRegion(id + "F16", true);
            var Q1;
            Q1=makeQuery(id+"F2.opExtrude","CAP_FACE",FACE,{"disambiguationData":[OSD([sQuery(id+"F0.wireOp",EDGE,"E12"),sQuery(id+"F0.wireOp",EDGE,"E13"),sQuery(id+"F0.wireOp",EDGE,"E14"),sQuery(id+"F0.wireOp",EDGE,"E15"),sQuery(id+"F0.wireOp",EDGE,"E17.filletArc"),sQuery(id+"F0.wireOp",EDGE,"E18.filletArc"),sQuery(id+"F0.wireOp",EDGE,"E19.filletArc"),sQuery(id+"F0.wireOp",EDGE,"E20.filletArc"),sQuery(id+"F0.wireOp",EDGE,"E25.0"),sQuery(id+"F0.wireOp",EDGE,"E25.1"),sQuery(id+"F0.wireOp",EDGE,"E25.2"),sQuery(id+"F0.wireOp",EDGE,"E25.3"),sQuery(id+"F0.wireOp",EDGE,"E25.4"),sQuery(id+"F0.wireOp",EDGE,"E25.5"),sQuery(id+"F0.wireOp",EDGE,"E25.6"),sQuery(id+"F0.wireOp",EDGE,"E25.7")])],"isStart":false});
            extrude(context, id + "F17", {"entities" : qUnion([Q0]), "endBound" : BoundingType.UP_TO_SURFACE, "depth" : 25 * mm, "endBoundEntityFace" : qUnion([Q1]), "offsetDistance" : 25 * mm});
        }
    });
